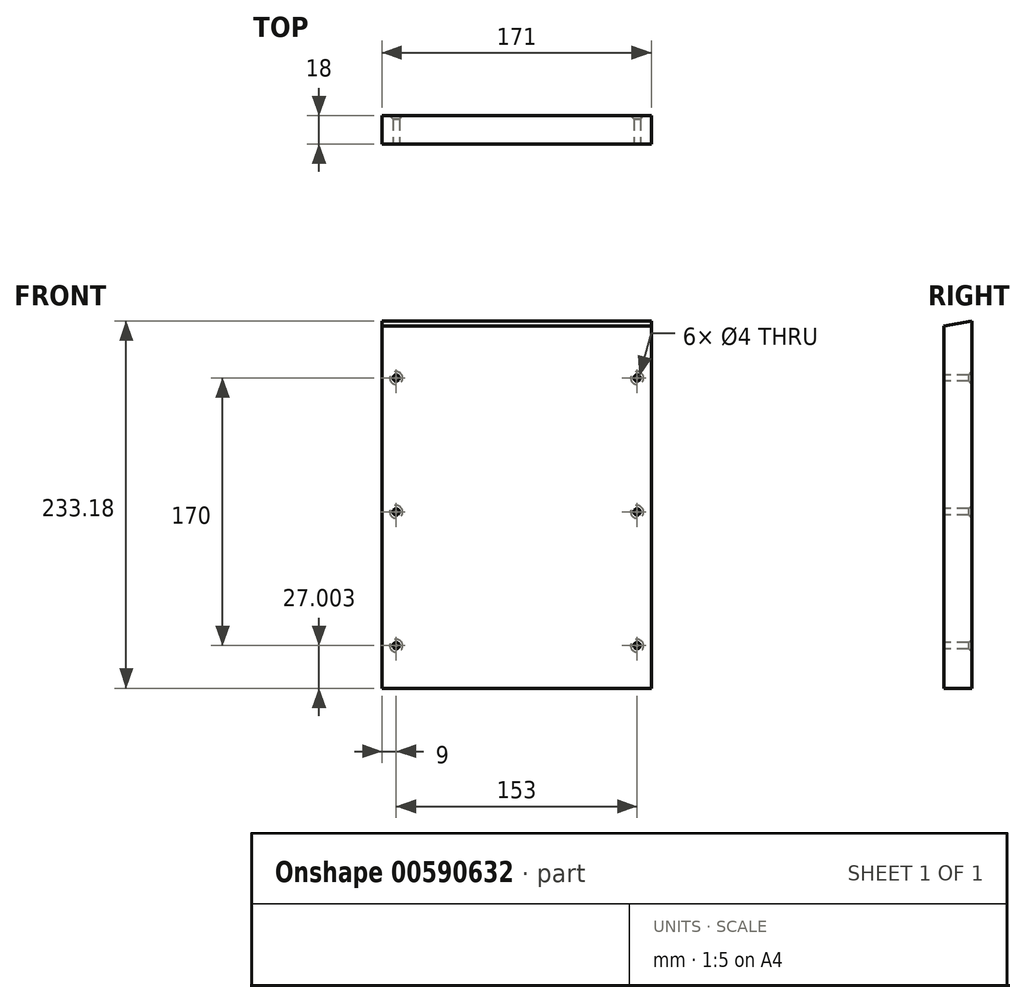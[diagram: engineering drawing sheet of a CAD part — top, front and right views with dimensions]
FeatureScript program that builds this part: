
annotation { "Feature Type Name" : "Feature", "Feature Type Description" : "" }
export const myFeature = defineFeature(function(context is Context, id is Id, definition is map)
    precondition{}
    {
        {
            var Q0;
            Q0=qCreatedBy(makeId("Front.planeOp"),FACE);
            var sketch = newSketch(context, id + "F0", { "sketchPlane" : qUnion([Q0])});
            skLineSegment(sketch, "E0.bottom", {"start": v(85.5, 116.59) * mm, "end": v(-85.5, 116.59) * mm});
            skLineSegment(sketch, "E0.top", {"start": v(85.5, -116.59) * mm, "end": v(-85.5, -116.59) * mm});
            skLineSegment(sketch, "E0.left", {"start": v(85.5, 116.59) * mm, "end": v(85.5, -116.59) * mm});
            skLineSegment(sketch, "E0.right", {"start": v(-85.5, 116.59) * mm, "end": v(-85.5, -116.59) * mm});
            skPoint(sketch, "E0.middle", {"position": v(0, 0) * mm});
            skSolve(sketch);
        }
        {
            var Q0;
            Q0=makeQuery(id+"F0.imprint","IMPRINT",FACE,{"disambiguationData":[TD([[makeQuery(id+"F0.imprint","IMPRINT",EDGE,{"derivedFrom":sQuery(id+"F0.wireOp",EDGE,"E0.bottom")}),1.0]])]});
            extrude(context, id + "F1", {"entities" : qUnion([Q0]), "depth" : 18 * mm, "offsetDistance" : 25 * mm});
        }
        {
            var Q0;
            Q0=makeQuery(id+"F1.opExtrude","SWEPT_FACE",FACE,{"disambiguationData":[OSD([sQuery(id+"F0.wireOp",EDGE,"E0.left")])]});
            var sketch = newSketch(context, id + "F2", { "sketchPlane" : qUnion([Q0])});
            skLineSegment(sketch, "E1", {"start": v(0, 116.59) * mm, "end": v(-18, 113.41) * mm});
            skLineSegment(sketch, "E2", {"start": v(-18, 116.59) * mm, "end": v(-18, 113.41) * mm});
            skLineSegment(sketch, "E3", {"start": v(0, 116.59) * mm, "end": v(-18, 116.59) * mm});
            skSolve(sketch);
        }
        {
            var Q0;
            Q0=makeQuery(id+"F2.imprint","IMPRINT",FACE,{"disambiguationData":[TD([[makeQuery(id+"F2.imprint","IMPRINT",EDGE,{"derivedFrom":sQuery(id+"F2.wireOp",EDGE,"E1")}),-1.0]])]});
            extrude(context, id + "F3", {"entities" : qUnion([Q0]), "operationType" : NewBodyOperationType.REMOVE, "endBound" : BoundingType.THROUGH_ALL, "oppositeDirection" : true, "depth" : 25 * mm, "offsetDistance" : 25 * mm});
        }
        {
            var Q0;
            Q0=makeQuery(id+"F0.imprint","IMPRINT",FACE,{"disambiguationData":[TD([[makeQuery(id+"F0.imprint","IMPRINT",EDGE,{"derivedFrom":sQuery(id+"F0.wireOp",EDGE,"E0.bottom")}),1.0]])]});
            var sketch = newSketch(context, id + "F4", { "sketchPlane" : qUnion([Q0])});
            skPoint(sketch, "E4", {"position": v(76.5, -89.59) * mm});
            skPoint(sketch, "E5", {"position": v(-76.5, -89.59) * mm});
            skPoint(sketch, "E6", {"position": v(76.5, -4.59) * mm});
            skPoint(sketch, "E7", {"position": v(-76.5, -4.59) * mm});
            skPoint(sketch, "E8", {"position": v(76.5, 80.41) * mm});
            skPoint(sketch, "E9", {"position": v(-76.5, 80.41) * mm});
            skSolve(sketch);
        }
        {
            var Q0;
            Q0=sQuery(id+"F4.wireOp",VERTEX,"E8");
            var Q1;
            Q1=sQuery(id+"F4.wireOp",VERTEX,"E9");
            var Q2;
            Q2=sQuery(id+"F4.wireOp",VERTEX,"E6");
            var Q3;
            Q3=sQuery(id+"F4.wireOp",VERTEX,"E7");
            var Q4;
            Q4=sQuery(id+"F4.wireOp",VERTEX,"E4");
            var Q5;
            Q5=sQuery(id+"F4.wireOp",VERTEX,"53fe51ca-8971-4553-968b-496b67f4d6cb");
            var Q6;
            Q6=sQuery(id+"F4.wireOp",VERTEX,"E5");
            var Q7;
            Q7=makeQuery(id+"F1.opExtrude","SWEPT_BODY",BODY,{"disambiguationData":[OSD([sQuery(id+"F0.wireOp",EDGE,"E0.bottom"),sQuery(id+"F0.wireOp",EDGE,"E0.top"),sQuery(id+"F0.wireOp",EDGE,"E0.left"),sQuery(id+"F0.wireOp",EDGE,"E0.right")])]});
            hole(context, id + "F5", {"style" : HoleStyle.C_SINK, "endStyle" : HoleEndStyle.THROUGH, "oppositeDirection" : true, "holeDiameter" : 4 * mm, "cSinkDiameter" : 8.2 * mm, "cSinkAngle" : 90 * degree, "majorDiameter" : 5 * mm, "isTappedThrough" : true, "tappedDepth" : 12 * mm, "tapClearance" : 3, "locations" : qUnion([Q0, Q1, Q2, Q3, Q4, Q5, Q6]), "scope" : qUnion([Q7])});
        }
    });
